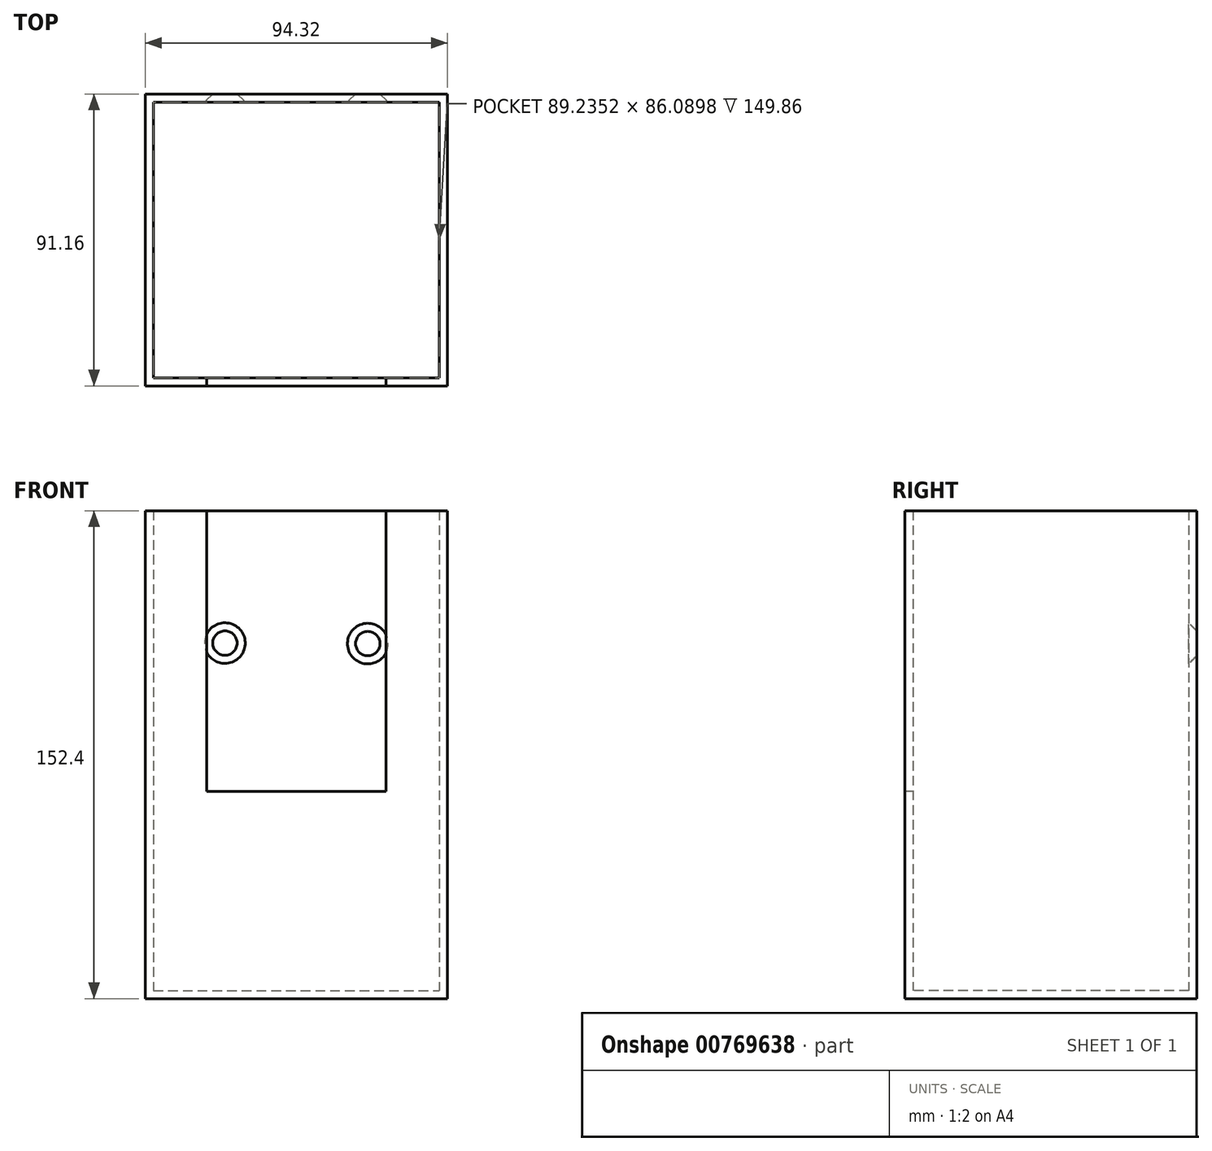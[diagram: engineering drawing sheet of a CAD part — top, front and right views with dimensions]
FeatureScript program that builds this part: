
annotation { "Feature Type Name" : "Feature", "Feature Type Description" : "" }
export const myFeature = defineFeature(function(context is Context, id is Id, definition is map)
    precondition{}
    {
        {
            var Q0;
            Q0=qCreatedBy(makeId("Top.planeOp"),FACE);
            var sketch = newSketch(context, id + "F0", { "sketchPlane" : qUnion([Q0])});
            skLineSegment(sketch, "E0.bottom", {"start": v(-47.16, 45.58) * mm, "end": v(47.16, 45.58) * mm});
            skLineSegment(sketch, "E0.top", {"start": v(-47.16, -45.58) * mm, "end": v(47.16, -45.58) * mm});
            skLineSegment(sketch, "E0.left", {"start": v(-47.16, 45.58) * mm, "end": v(-47.16, -45.58) * mm});
            skLineSegment(sketch, "E0.right", {"start": v(47.16, 45.58) * mm, "end": v(47.16, -45.58) * mm});
            skPoint(sketch, "E0.middle", {"position": v(0, 0) * mm});
            skSolve(sketch);
        }
        {
            var Q0;
            Q0 = qSketchRegion(id + "F0", true);
            extrude(context, id + "F1", {"entities" : qUnion([Q0]), "depth" : 152.4 * mm, "offsetDistance" : 25.4 * mm});
        }
        {
            var Q0;
            Q0=makeQuery(id+"F1.opExtrude","SWEPT_FACE",FACE,{"disambiguationData":[OSD([sQuery(id+"F0.wireOp",EDGE,"E0.top")])]});
            var sketch = newSketch(context, id + "F2", { "sketchPlane" : qUnion([Q0])});
            skSolve(sketch);
        }
        {
            var Q0;
            {var subQ0=sQuery(id+"F0.wireOp",EDGE,"E0.top");Q0=makeQuery(id+"F2.imprint","IMPRINT",FACE,{"disambiguationData":[TD([[makeQuery(id+"F2.imprint","IMPRINT",EDGE,{"derivedFrom":makeQuery(id+"F1.opExtrude","CAP_EDGE",EDGE,{"disambiguationData":[OSD([subQ0])],"isStart":true})}),1.0]])]});}
            var sketch = newSketch(context, id + "F3", { "sketchPlane" : qUnion([Q0])});
            skLineSegment(sketch, "E1.bottom", {"start": v(19.54, 48.72) * mm, "end": v(-19.54, 48.72) * mm});
            skLineSegment(sketch, "E1.top", {"start": v(25.9, 258.65) * mm, "end": v(-25.9, 258.65) * mm});
            skLineSegment(sketch, "E1.left", {"start": v(25.9, 55.07) * mm, "end": v(25.9, 258.65) * mm});
            skLineSegment(sketch, "E1.right", {"start": v(-25.9, 55.07) * mm, "end": v(-25.9, 258.65) * mm});
            skPoint(sketch, "E1.middle", {"position": v(0, 153.68) * mm});
            skPoint(sketch, "E2.visualSharp", {"position": v(-25.9, 48.72) * mm});
            skArc(sketch, "E2.filletArc", {"start": v(-25.9, 55.07) * mm, "mid": v(-24.03, 50.58) * mm, "end": v(-19.54, 48.72) * mm});
            skPoint(sketch, "E3.visualSharp", {"position": v(25.9, 48.72) * mm});
            skArc(sketch, "E3.filletArc", {"start": v(19.54, 48.72) * mm, "mid": v(24.03, 50.58) * mm, "end": v(25.9, 55.07) * mm});
            skSolve(sketch);
        }
        {
            var Q0;
            Q0=makeQuery(id+"F1.opExtrude","CAP_FACE",FACE,{"disambiguationData":[OSD([sQuery(id+"F0.wireOp",EDGE,"E0.bottom"),sQuery(id+"F0.wireOp",EDGE,"E0.top"),sQuery(id+"F0.wireOp",EDGE,"E0.left"),sQuery(id+"F0.wireOp",EDGE,"E0.right")])],"isStart":false});
            shell(context, id + "F4", {"entities" : qUnion([Q0]), "thickness" : 2.54 * mm});
        }
        {
            var Q0;
            {var subQ0=sQuery(id+"F3.wireOp",EDGE,"E1.bottom");Q0=makeQuery(id+"F3.imprint","IMPRINT",FACE,{"disambiguationData":[TD([[makeQuery(id+"F3.imprint","IMPRINT",EDGE,{"derivedFrom":subQ0}),-1.0]])]});}
            var sketch = newSketch(context, id + "F5", { "sketchPlane" : qUnion([Q0])});
            skLineSegment(sketch, "E4.bottom", {"start": v(28.06, 64.75) * mm, "end": v(-28.06, 64.75) * mm});
            skLineSegment(sketch, "E4.top", {"start": v(28.06, 245.96) * mm, "end": v(-28.06, 245.96) * mm});
            skLineSegment(sketch, "E4.left", {"start": v(28.06, 64.75) * mm, "end": v(28.06, 245.96) * mm});
            skLineSegment(sketch, "E4.right", {"start": v(-28.06, 64.75) * mm, "end": v(-28.06, 245.96) * mm});
            skPoint(sketch, "E4.middle", {"position": v(0, 155.35) * mm});
            skSolve(sketch);
        }
        {
            var Q0;
            Q0 = qSketchRegion(id + "F5", true);
            extrude(context, id + "F6", {"entities" : qUnion([Q0]), "operationType" : NewBodyOperationType.REMOVE, "oppositeDirection" : true, "depth" : 25.4 * mm, "offsetDistance" : 25.4 * mm});
        }
        {
            var Q0;
            Q0=makeQuery(id+"F4.opShell","OFFSET_FACE",FACE,{"disambiguationData":[OSD([sQuery(id+"F0.wireOp",EDGE,"E0.bottom")])]});
            var sketch = newSketch(context, id + "F7", { "sketchPlane" : qUnion([Q0])});
            skLineSegment(sketch, "E5", {"start": v(0, 152.4) * mm, "end": v(-44.62, 152.4) * mm});
            skLineSegment(sketch, "E6", {"start": v(-44.62, 152.4) * mm, "end": v(-22.3, 152.4) * mm});
            skCircle(sketch, "E7", {"center": v(-22.3, 111.04) * mm, "radius": 3.4 * mm});
            skSolve(sketch);
        }
        {
            var Q0;
            Q0=sQuery(id+"F7.wireOp",VERTEX,"E7.center");
            var Q1;
            Q1=makeQuery(id+"F1.opExtrude","SWEPT_BODY",BODY,{"disambiguationData":[OSD([sQuery(id+"F0.wireOp",EDGE,"E0.bottom"),sQuery(id+"F0.wireOp",EDGE,"E0.top"),sQuery(id+"F0.wireOp",EDGE,"E0.left"),sQuery(id+"F0.wireOp",EDGE,"E0.right")])]});
            hole(context, id + "F8", {"style" : HoleStyle.C_SINK, "endStyle" : HoleEndStyle.THROUGH, "holeDiameter" : 6.35 * mm, "cSinkDiameter" : 12.7 * mm, "cSinkAngle" : 90 * degree, "majorDiameter" : 6.35 * mm, "isTappedThrough" : true, "tappedDepth" : 12.7 * mm, "tapClearance" : 3, "locations" : qUnion([Q0]), "scope" : qUnion([Q1])});
        }
        {
            var Q0;
            Q0=makeQuery(id+"F4.opShell","OFFSET_FACE",FACE,{"disambiguationData":[OSD([sQuery(id+"F0.wireOp",EDGE,"E0.bottom")])]});
            var sketch = newSketch(context, id + "F9", { "sketchPlane" : qUnion([Q0])});
            skLineSegment(sketch, "E8", {"start": v(44.62, 152.4) * mm, "end": v(0, 152.4) * mm});
            skLineSegment(sketch, "E9", {"start": v(0, 152.4) * mm, "end": v(22.3, 152.4) * mm});
            skLineSegment(sketch, "E10", {"start": v(-28.66, 110.89) * mm, "end": v(40.77, 110.89) * mm});
            skLineSegment(sketch, "E11", {"start": v(22.3, 152.4) * mm, "end": v(22.3, 91.9) * mm});
            skCircle(sketch, "E12", {"center": v(22.3, 110.89) * mm, "radius": 4.68 * mm});
            skSolve(sketch);
        }
        {
            var Q0;
            Q0=sQuery(id+"F9.wireOp",VERTEX,"E12.center");
            var Q1;
            Q1=makeQuery(id+"F1.opExtrude","SWEPT_BODY",BODY,{"disambiguationData":[OSD([sQuery(id+"F0.wireOp",EDGE,"E0.bottom"),sQuery(id+"F0.wireOp",EDGE,"E0.top"),sQuery(id+"F0.wireOp",EDGE,"E0.left"),sQuery(id+"F0.wireOp",EDGE,"E0.right")])]});
            hole(context, id + "F10", {"style" : HoleStyle.C_SINK, "endStyle" : HoleEndStyle.THROUGH, "holeDiameter" : 6.35 * mm, "cSinkDiameter" : 12.7 * mm, "cSinkAngle" : 90 * degree, "majorDiameter" : 6.35 * mm, "isTappedThrough" : true, "tappedDepth" : 12.7 * mm, "tapClearance" : 3, "locations" : qUnion([Q0]), "scope" : qUnion([Q1])});
        }
    });
